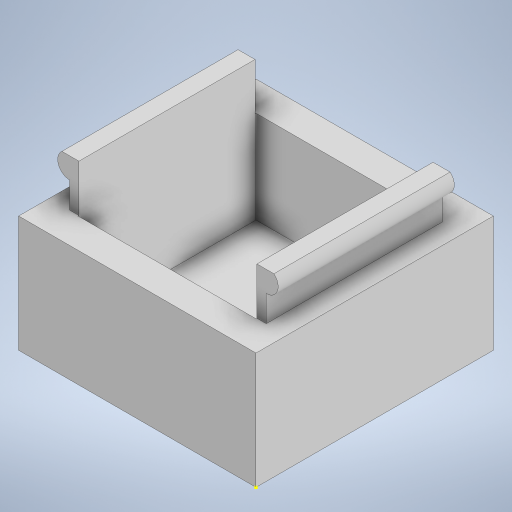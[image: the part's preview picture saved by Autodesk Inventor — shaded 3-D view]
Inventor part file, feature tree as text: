
AUTODESK INVENTOR PART (.ipt)
format: ipt  version: 2023 (Build 270158000, 158)  size: 268,288 bytes
history: native  units: in
note: dims shown in document units (in); Inventor stores cm internally (conversion verified against a paired STEP export)
features: sketch x6, extrude x5
ambient origin geometry x8: Origin, YZ Plane, XZ Plane, XY Plane, X Axis, Y Axis, Z Axis, Center Point
bodies: Solid1 (feature_tree)
feature tree (11):
  sketch  "Sketch1"  dims[d0=1.0in d1=1.0in]
  extrude  "Extrusion1"  Depth=1.0in
  extrude  "Extrusion2"  Depth=0.125in
  extrude  "Extrusion3"  Depth=0.125in
  extrude  "Extrusion4"  Depth=0.125in TaperAngle=0.0deg
  extrude  "Extrusion5"  Depth=0.1in
  sketch  "Sketch2"  dims[d2=0.7in d3=0.0in d4=0.125in]
  sketch  "Sketch3"  dims[d5=0.125in d6=0.125in]
  sketch  "Sketch4"  dims[d7=0.125in d8=0.6in d9=0.0in]
  sketch  "Sketch5"  dims[d10=0.1in d11=0.1in]
  sketch  "Sketch6"  dims[d12=0.05in d13=0.05in d14=0.0394in d15=0.0394in d16=0.0394in d17=0.21in d18=0.0394in d19=0.21in d20=1.0in d21=0.0in d22=1.0in d23=0.0in d25=0.1289in d26=0.1289in d27=0.0118in d28=0.0in d29=1.1811in d30=1.0in d31=0.0in]
